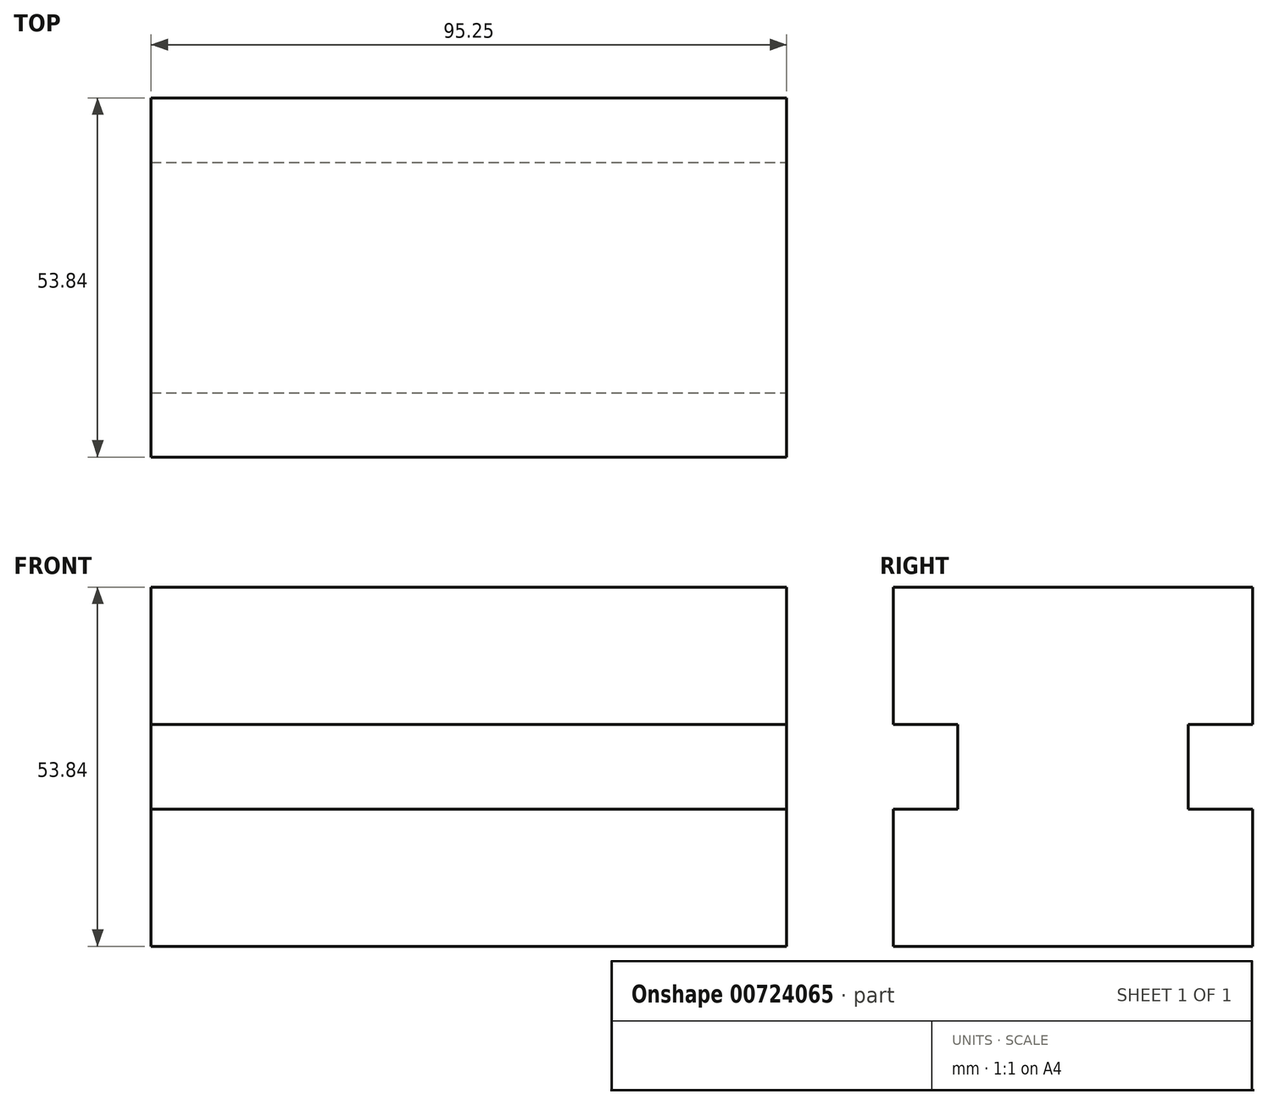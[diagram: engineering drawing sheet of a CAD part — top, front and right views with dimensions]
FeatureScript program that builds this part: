
annotation { "Feature Type Name" : "Feature", "Feature Type Description" : "" }
export const myFeature = defineFeature(function(context is Context, id is Id, definition is map)
    precondition{}
    {
        {
            var Q0;
            Q0=qCreatedBy(makeId("Right.planeOp"),FACE);
            var sketch = newSketch(context, id + "F0", { "sketchPlane" : qUnion([Q0])});
            skLineSegment(sketch, "E0.bottom", {"start": v(26.92, -26.92) * mm, "end": v(-26.92, -26.92) * mm});
            skLineSegment(sketch, "E0.top", {"start": v(26.92, 26.92) * mm, "end": v(-26.92, 26.92) * mm});
            skLineSegment(sketch, "E0.left", {"start": v(26.92, -26.92) * mm, "end": v(26.92, -6.35) * mm});
            skLineSegment(sketch, "E0.right", {"start": v(-26.92, -26.92) * mm, "end": v(-26.92, -6.35) * mm});
            skPoint(sketch, "E0.middle", {"position": v(0, 0) * mm});
            skLineSegment(sketch, "E1.bottom", {"start": v(-26.92, -6.35) * mm, "end": v(-17.27, -6.35) * mm});
            skLineSegment(sketch, "E1.top", {"start": v(-26.92, 6.35) * mm, "end": v(-17.27, 6.35) * mm});
            skLineSegment(sketch, "E1.right", {"start": v(-17.27, -6.35) * mm, "end": v(-17.27, 6.35) * mm});
            skLineSegment(sketch, "E2.trimOffspring", {"start": v(-26.92, 6.35) * mm, "end": v(-26.92, 26.92) * mm});
            skLineSegment(sketch, "E3", {"start": v(0, 42.68) * mm, "end": v(0, -37.33) * mm, "construction": true});
            skLineSegment(sketch, "E4.MirrorCS", {"start": v(26.92, 6.35) * mm, "end": v(17.27, 6.35) * mm});
            skLineSegment(sketch, "E5.MirrorCS", {"start": v(17.27, -6.35) * mm, "end": v(17.27, 6.35) * mm});
            skLineSegment(sketch, "E6.MirrorCS", {"start": v(26.92, -6.35) * mm, "end": v(17.27, -6.35) * mm});
            skLineSegment(sketch, "E7.trimOffspring", {"start": v(26.92, 6.35) * mm, "end": v(26.92, 26.92) * mm});
            skSolve(sketch);
        }
        {
            var Q0;
            Q0=makeQuery(id+"F0.imprint","IMPRINT",FACE,{"disambiguationData":[TD([[makeQuery(id+"F0.imprint","IMPRINT",EDGE,{"derivedFrom":sQuery(id+"F0.wireOp",EDGE,"E0.bottom")}),-1.0]])]});
            extrude(context, id + "F1", {"entities" : qUnion([Q0]), "oppositeDirection" : true, "depth" : 95.25 * mm, "offsetDistance" : 25.4 * mm});
        }
    });
